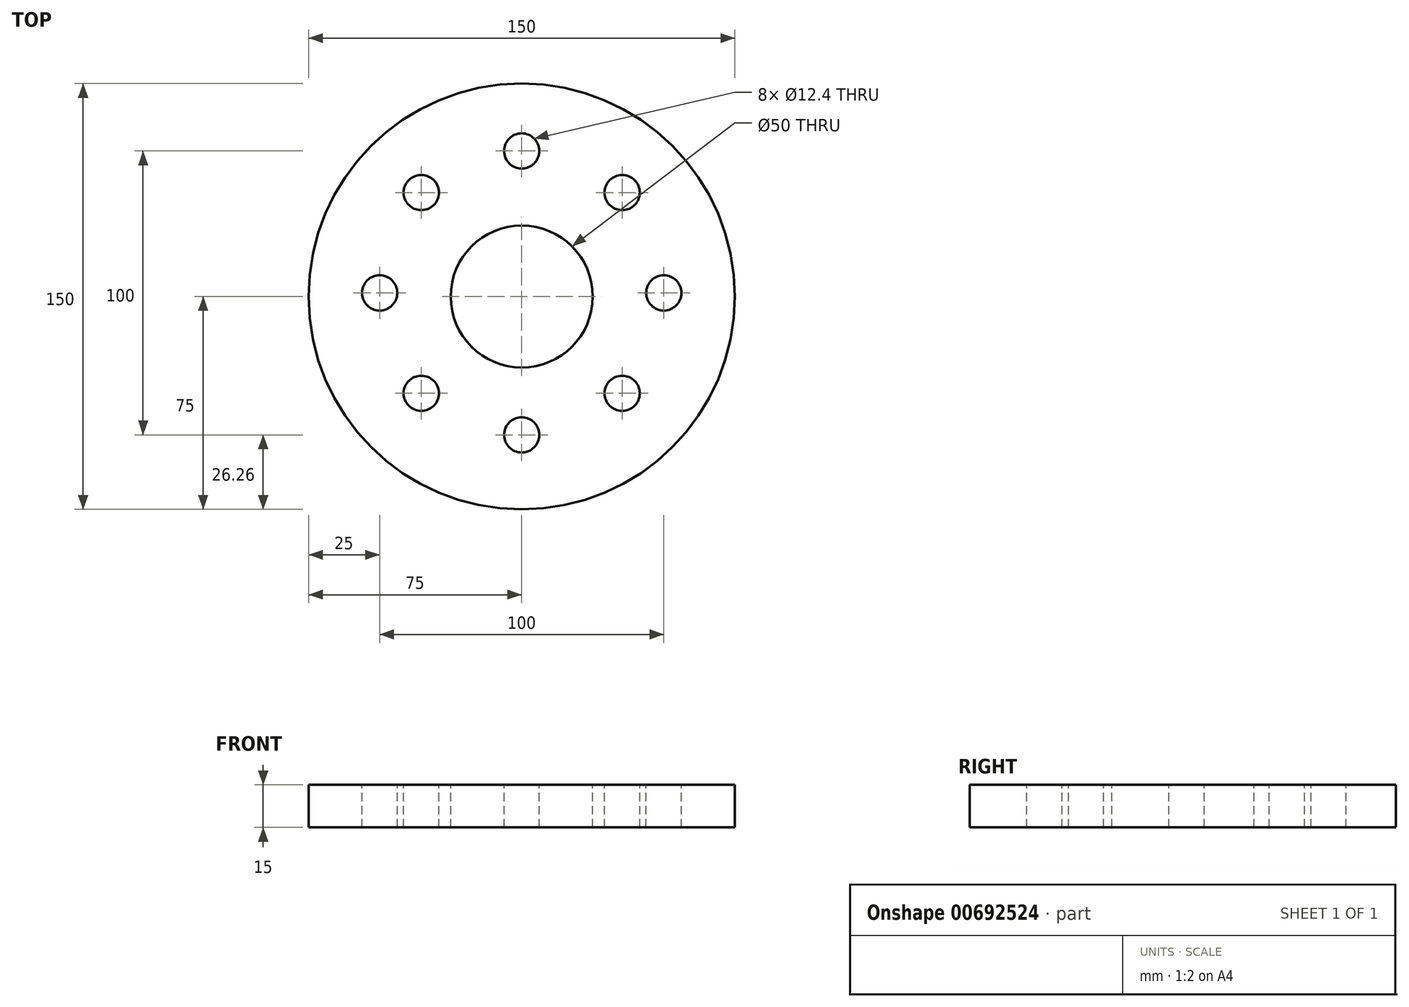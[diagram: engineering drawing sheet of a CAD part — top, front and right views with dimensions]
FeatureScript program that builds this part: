
annotation { "Feature Type Name" : "Feature", "Feature Type Description" : "" }
export const myFeature = defineFeature(function(context is Context, id is Id, definition is map)
    precondition{}
    {
        {
            var Q0;
            Q0=qCreatedBy(makeId("Top.planeOp"),FACE);
            var sketch = newSketch(context, id + "F0", { "sketchPlane" : qUnion([Q0])});
            skCircle(sketch, "E0", {"center": v(0, 0) * mm, "radius": 75 * mm});
            skSolve(sketch);
        }
        {
            var Q0;
            Q0 = qSketchRegion(id + "F0", true);
            extrude(context, id + "F1", {"entities" : qUnion([Q0]), "depth" : 15 * mm, "offsetDistance" : 25 * mm});
        }
        {
            var Q0;
            Q0=makeQuery(id+"F1.opExtrude","CAP_FACE",FACE,{"disambiguationData":[OSD([sQuery(id+"F0.wireOp",EDGE,"E0")])],"isStart":false});
            var sketch = newSketch(context, id + "F2", { "sketchPlane" : qUnion([Q0])});
            skCircle(sketch, "E1", {"center": v(0, 51.26) * mm, "radius": 6.2 * mm});
            skCircle(sketch, "E2.1.0", {"center": v(-35.36, 36.62) * mm, "radius": 6.2 * mm});
            skCircle(sketch, "E2.2.0", {"center": v(-50, 1.26) * mm, "radius": 6.2 * mm});
            skCircle(sketch, "E2.3.0", {"center": v(-35.36, -34.1) * mm, "radius": 6.2 * mm});
            skPoint(sketch, "E2.center", {"position": v(0, 1.26) * mm});
            skCircle(sketch, "E3.1.4.0", {"center": v(0, -48.74) * mm, "radius": 6.2 * mm});
            skCircle(sketch, "E3.1.5.0", {"center": v(35.36, -34.1) * mm, "radius": 6.2 * mm});
            skCircle(sketch, "E3.1.6.0", {"center": v(50, 1.26) * mm, "radius": 6.2 * mm});
            skCircle(sketch, "E3.1.7.0", {"center": v(35.36, 36.62) * mm, "radius": 6.2 * mm});
            skSolve(sketch);
        }
        {
            var Q0;
            Q0=makeQuery(id+"F2.imprint","IMPRINT",FACE,{"disambiguationData":[TD([[makeQuery(id+"F2.imprint","IMPRINT",EDGE,{"derivedFrom":sQuery(id+"F2.wireOp",EDGE,"E1")}),1.0]])]});
            var Q1;
            Q1=makeQuery(id+"F2.imprint","IMPRINT",FACE,{"disambiguationData":[TD([[makeQuery(id+"F2.imprint","IMPRINT",EDGE,{"derivedFrom":sQuery(id+"F2.wireOp",EDGE,"E2.3.0")}),1.0]])]});
            var Q2;
            Q2=makeQuery(id+"F2.imprint","IMPRINT",FACE,{"disambiguationData":[TD([[makeQuery(id+"F2.imprint","IMPRINT",EDGE,{"derivedFrom":sQuery(id+"F2.wireOp",EDGE,"E2.2.0")}),1.0]])]});
            var Q3;
            Q3=makeQuery(id+"F2.imprint","IMPRINT",FACE,{"disambiguationData":[TD([[makeQuery(id+"F2.imprint","IMPRINT",EDGE,{"derivedFrom":sQuery(id+"F2.wireOp",EDGE,"E2.1.0")}),1.0]])]});
            var Q4;
            Q4=makeQuery(id+"F2.imprint","IMPRINT",FACE,{"disambiguationData":[TD([[makeQuery(id+"F2.imprint","IMPRINT",EDGE,{"derivedFrom":sQuery(id+"F2.wireOp",EDGE,"E3.1.4.0")}),1.0]])]});
            var Q5;
            Q5=makeQuery(id+"F2.imprint","IMPRINT",FACE,{"disambiguationData":[TD([[makeQuery(id+"F2.imprint","IMPRINT",EDGE,{"derivedFrom":sQuery(id+"F2.wireOp",EDGE,"E3.1.5.0")}),1.0]])]});
            var Q6;
            Q6=makeQuery(id+"F2.imprint","IMPRINT",FACE,{"disambiguationData":[TD([[makeQuery(id+"F2.imprint","IMPRINT",EDGE,{"derivedFrom":sQuery(id+"F2.wireOp",EDGE,"E3.1.6.0")}),1.0]])]});
            var Q7;
            Q7=makeQuery(id+"F2.imprint","IMPRINT",FACE,{"disambiguationData":[TD([[makeQuery(id+"F2.imprint","IMPRINT",EDGE,{"derivedFrom":sQuery(id+"F2.wireOp",EDGE,"E3.1.7.0")}),1.0]])]});
            extrude(context, id + "F3", {"entities" : qUnion([Q0, Q1, Q2, Q3, Q4, Q5, Q6, Q7]), "operationType" : NewBodyOperationType.REMOVE, "oppositeDirection" : true, "depth" : 25 * mm, "offsetDistance" : 25 * mm});
        }
        {
            var Q0;
            Q0=makeQuery(id+"F1.opExtrude","CAP_FACE",FACE,{"disambiguationData":[OSD([sQuery(id+"F0.wireOp",EDGE,"E0")])],"isStart":false});
            var sketch = newSketch(context, id + "F4", { "sketchPlane" : qUnion([Q0])});
            skCircle(sketch, "E4", {"center": v(0, 0) * mm, "radius": 25 * mm});
            skSolve(sketch);
        }
        {
            var Q0;
            Q0=makeQuery(id+"F4.imprint","IMPRINT",FACE,{"disambiguationData":[TD([[makeQuery(id+"F4.imprint","IMPRINT",EDGE,{"derivedFrom":sQuery(id+"F4.wireOp",EDGE,"E4")}),1.0]])]});
            extrude(context, id + "F5", {"entities" : qUnion([Q0]), "operationType" : NewBodyOperationType.REMOVE, "oppositeDirection" : true, "depth" : 25 * mm, "offsetDistance" : 25 * mm});
        }
    });
